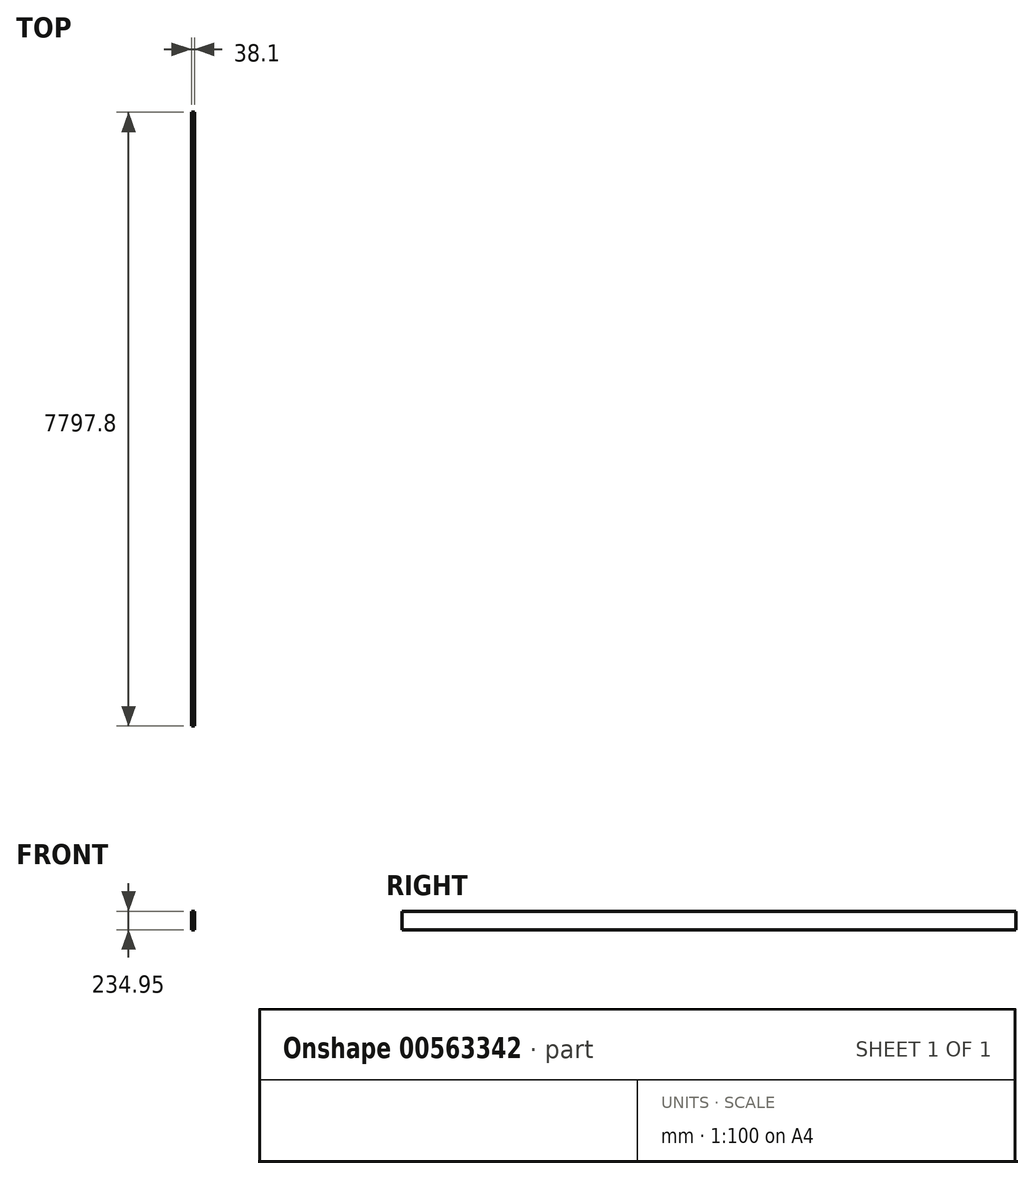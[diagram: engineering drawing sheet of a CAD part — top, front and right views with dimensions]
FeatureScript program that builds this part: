
annotation { "Feature Type Name" : "Feature", "Feature Type Description" : "" }
export const myFeature = defineFeature(function(context is Context, id is Id, definition is map)
    precondition{}
    {
        {
            var Q0;
            Q0=qCreatedBy(makeId("Top.planeOp"),FACE);
            var sketch = newSketch(context, id + "F0", { "sketchPlane" : qUnion([Q0])});
            skLineSegment(sketch, "E0.bottom", {"start": v(-19.05, -3898.9) * mm, "end": v(19.05, -3898.9) * mm});
            skLineSegment(sketch, "E0.top", {"start": v(-19.05, 3898.9) * mm, "end": v(19.05, 3898.9) * mm});
            skLineSegment(sketch, "E0.left", {"start": v(-19.05, -3898.9) * mm, "end": v(-19.05, 3898.9) * mm});
            skLineSegment(sketch, "E0.right", {"start": v(19.05, -3898.9) * mm, "end": v(19.05, 3898.9) * mm});
            skPoint(sketch, "E0.middle", {"position": v(0, 0) * mm});
            skSolve(sketch);
        }
        {
            var Q0;
            Q0 = qSketchRegion(id + "F0", true);
            extrude(context, id + "F1", {"entities" : qUnion([Q0]), "depth" : 234.95 * mm, "offsetDistance" : 25.4 * mm});
        }
    });
